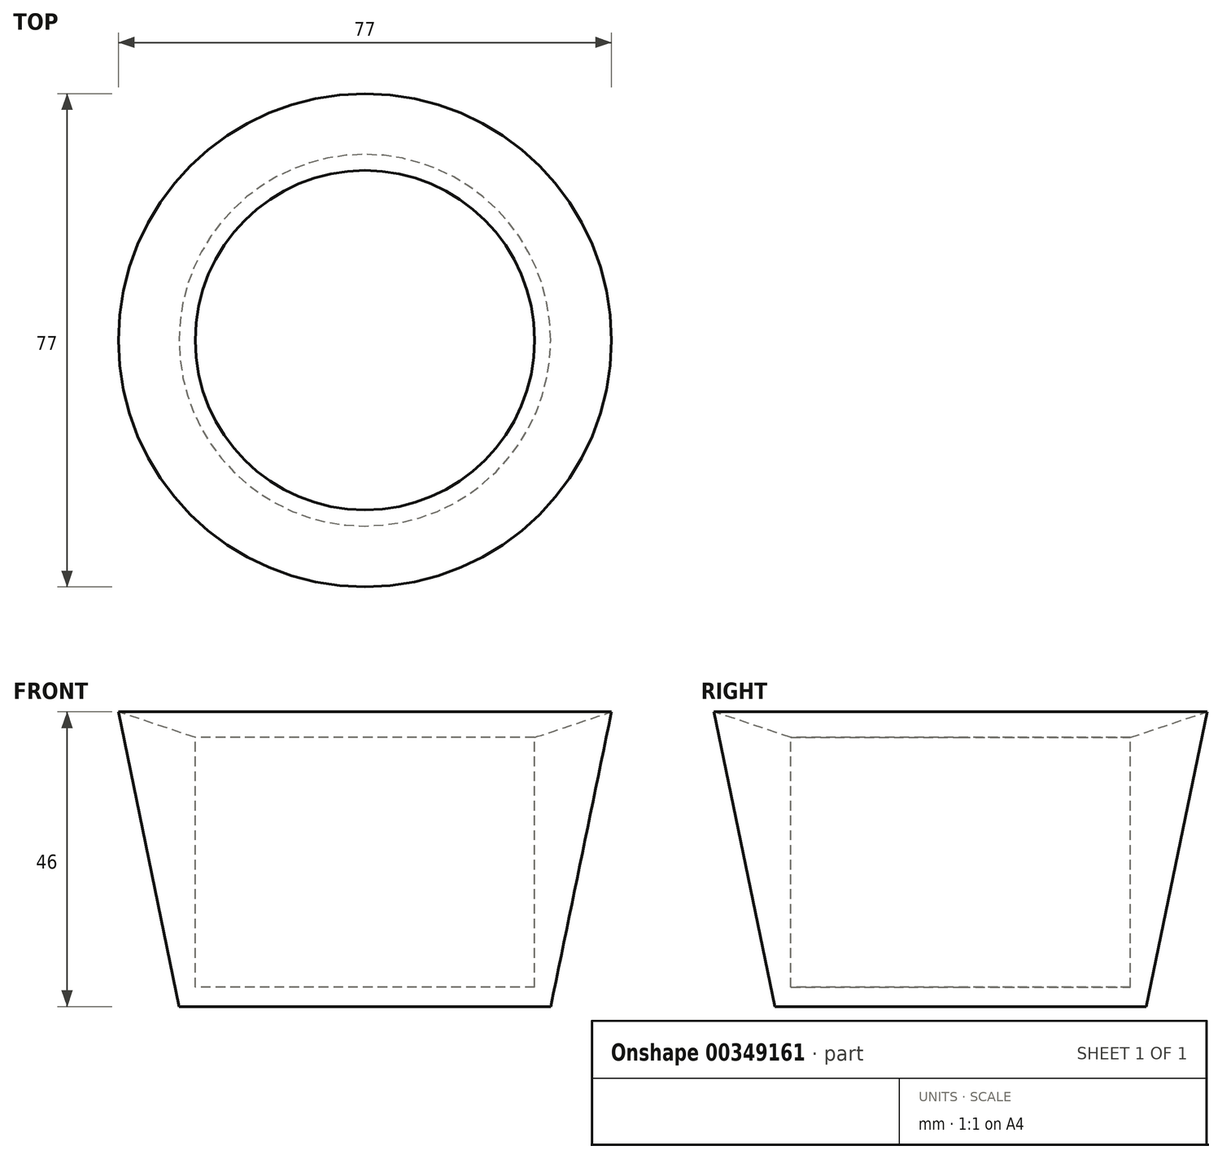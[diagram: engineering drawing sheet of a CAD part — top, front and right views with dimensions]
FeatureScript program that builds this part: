
annotation { "Feature Type Name" : "Feature", "Feature Type Description" : "" }
export const myFeature = defineFeature(function(context is Context, id is Id, definition is map)
    precondition{}
    {
        {
            var Q0;
            Q0=qCreatedBy(makeId("Right.planeOp"),FACE);
            var sketch = newSketch(context, id + "F0", { "sketchPlane" : qUnion([Q0])});
            skLineSegment(sketch, "E0", {"start": v(-38.5, 46) * mm, "end": v(-26.5, 42) * mm});
            skLineSegment(sketch, "E1", {"start": v(-26.5, 42) * mm, "end": v(-26.5, 3) * mm});
            skLineSegment(sketch, "E2", {"start": v(-26.5, 3) * mm, "end": v(0, 3) * mm});
            skLineSegment(sketch, "E3", {"start": v(0, 3) * mm, "end": v(0, 0) * mm});
            skLineSegment(sketch, "E4", {"start": v(0, 0) * mm, "end": v(-29, 0) * mm});
            skLineSegment(sketch, "E5", {"start": v(-29, 0) * mm, "end": v(-38.5, 46) * mm});
            skSolve(sketch);
        }
        {
            var Q0;
            Q0=makeQuery(id+"F0.imprint","IMPRINT",FACE,{"disambiguationData":[TD([[makeQuery(id+"F0.imprint","IMPRINT",EDGE,{"derivedFrom":sQuery(id+"F0.wireOp",EDGE,"E0")}),-1.0]])]});
            var Q1;
            Q1=sQuery(id+"F0.wireOp",EDGE,"E3");
            revolve(context, id + "F1", {"entities" : qUnion([Q0]), "axis" : qUnion([Q1]), "revolveType" : RevolveType.FULL});
        }
    });
